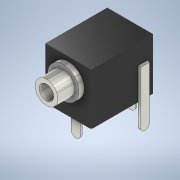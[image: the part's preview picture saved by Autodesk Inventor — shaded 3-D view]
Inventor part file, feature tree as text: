
AUTODESK INVENTOR PART (.ipt)
format: ipt  version: 2020 (Build 240168000, 168)  size: 210,432 bytes
history: native  units: mm
features: sketch x11, extrude x10, other x1
ambient origin geometry x8: Origin, YZ Plane, XZ Plane, XY Plane, X Axis, Y Axis, Z Axis, Center Point
bodies: Body1 (feature_tree)
feature tree (22):
  other  "Твердое тело1"
  extrude  "Выдавливание1"  Depth=10.8mm
  extrude  "Выдавливание2"  Depth=8.0mm
  extrude  "Выдавливание3"  Depth=9.0mm TaperAngle=0.0deg
  extrude  "Выдавливание4"  Depth=5.5mm
  sketch  "Эскиз5"
  extrude  "Выдавливание5"  Depth=4.0mm
  extrude  "Выдавливание6"  Depth=5.5mm
  extrude  "Выдавливание7"  Depth=0.9mm TaperAngle=0.0deg
  extrude  "Выдавливание8"  Depth=4.0mm
  extrude  "Выдавливание9"  Depth=2.95mm TaperAngle=0.0deg
  extrude  "Выдавливание10"  Depth=2.55mm
  sketch  "Эскиз1"
  sketch  "Эскиз2"
  sketch  "Эскиз3"
  sketch  "Эскиз4"
  sketch  "Эскиз6"
  sketch  "Эскиз7"
  sketch  "Эскиз8"
  sketch  "Эскиз9"
  sketch  "Эскиз10"
  sketch  "Эскиз11"
